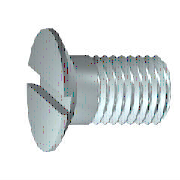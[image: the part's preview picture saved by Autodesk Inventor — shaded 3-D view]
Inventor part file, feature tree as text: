
AUTODESK INVENTOR PART (.ipt)
format: ipt  version: 2022 (Build 260153000, 153)  size: 180,736 bytes
history: native  units: mm (DEFAULTED — no unit token found)
features: sketch x2, extrude x1, plane x1
ambient origin geometry x7: Origin, YZ Plane, XZ Plane, X Axis, Y Axis, Z Axis, Center Point
bodies: Solid1 (feature_tree), Body (feature_tree)
feature tree (4):
  extrude  "Slot"  Depth=2.38655mm
  plane  "Work Plane1"
  sketch  "Sketch1"  dims[d0=8.0mm d1=45.0deg d2=0.306725mm d3=5.35mm d4=1.65mm d5=2.38655mm]
  sketch  "Sketch2"  dims[d6=3.0mm d7=5.5mm d19=90.0deg d8=0.85mm d9=0.0mm d10=5.35mm d11=0.0mm d12=0.306725mm d13=0.153363mm d15=1.0mm d16=5.5mm d17=0.0mm d35=45.0deg d39=0.0mm d40=0.0mm]
